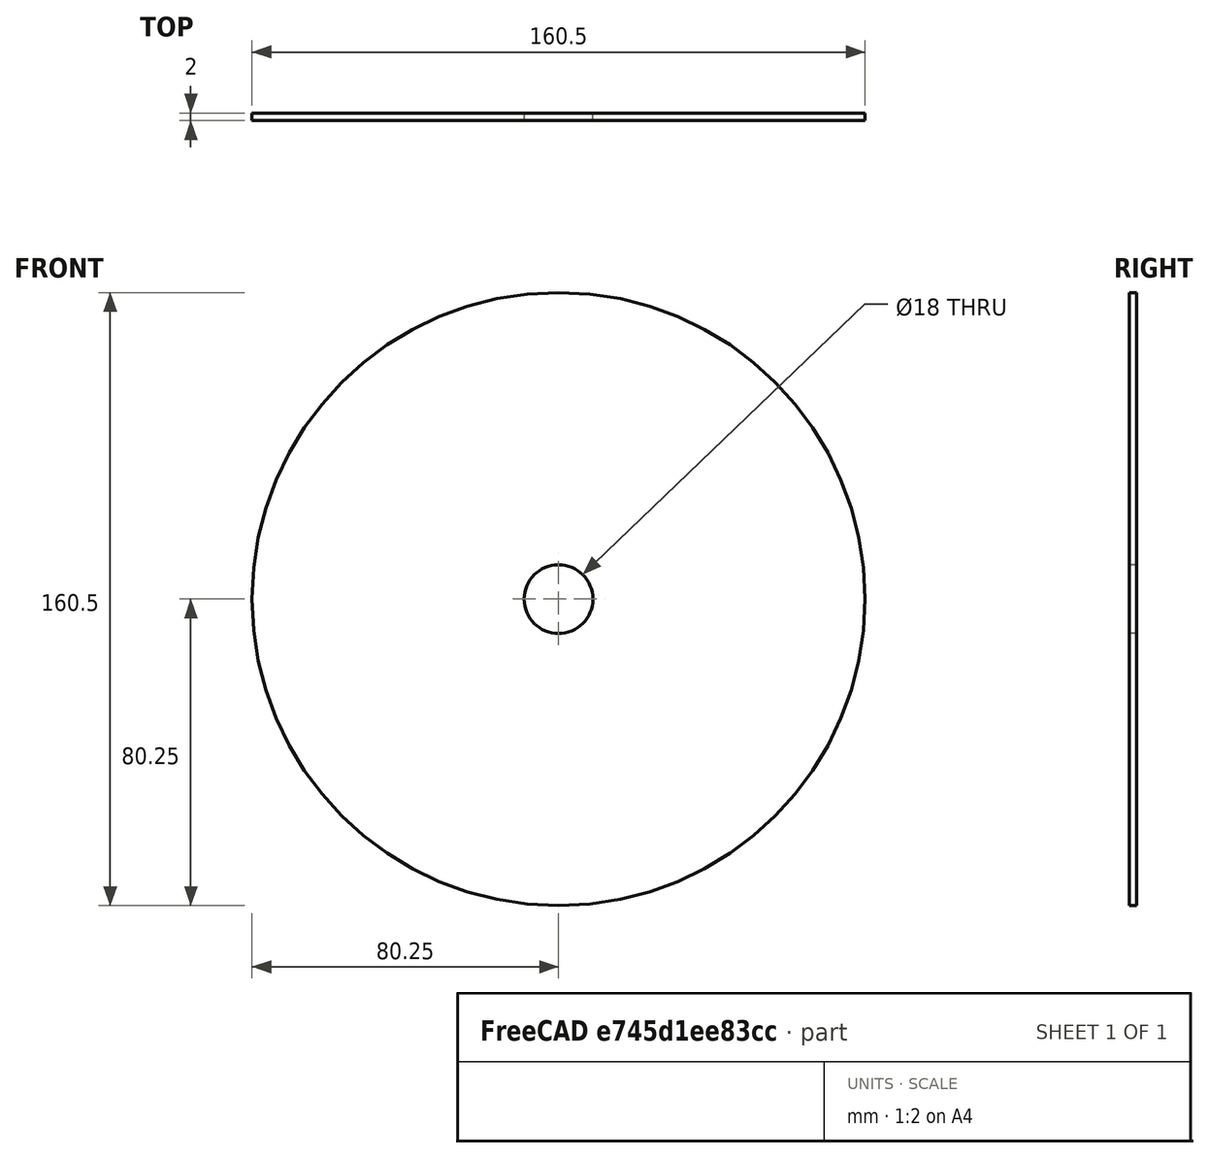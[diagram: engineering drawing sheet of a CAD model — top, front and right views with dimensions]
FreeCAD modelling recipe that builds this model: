
FCSTD DOCUMENT  (FreeCAD 0.21R33771 (Git))
Label: e1a24e2bb6364e30
License: All rights reserved
LicenseURL: https://en.wikipedia.org/wiki/All_rights_reserved
objects: Sketcher::SketchObject×2, TechDraw::DrawSVGTemplate×2, TechDraw::DrawViewPart×2, TechDraw::DrawPage×2, TechDraw::DrawViewDimExtent×2, Spreadsheet::Sheet×1, PartDesign::Pad×1, PartDesign::Pocket×1, PartDesign::Body×1
note: 9 computed .brp shape members not serialized (recipe doc carries the construction recipe); baked Part::Feature solids carry a one-line shape summary decoded from their .brp

FEATURE [Spreadsheet::Sheet] Spreadsheet  label="specification"
  cells = A1='Name ; B1(name)='Sägeblatt; A2='Beschreibung ; B2(description)='Sägeblatt für Harthölzer; A3='Typ ; B3(type)='SBHH; A4='Stammblattbreite (mm) ; B4(stammblattbreite)=2; A5='Plattensitzhöhe (mm) ; B5(plattensitzhoehe)=3.5; A6='Plattensitzlänge (mm) ; B6(plattensitzlaenge)=3.55; A7='Plattensitzwinkel (°) ; B7(plattensitzwinkel)=40.25; A8='Schnittbreite (mm) ; B8(schnittbreite)=3.2; A9='Außendurchmesser (mm) ; B9(aussendurchmesser)=160.5; A10='Bohrungsdurchmesser (mm) ; B10(bohrungsdurchmesser)=18; A11='Zähnezahl ; B11(zaehnezahl)=60
FEATURE [Sketcher::SketchObject] Sketch
  FullyConstrained = true
  MapMode = 5
  Placement = pos=(0,0,0) rot=(1,0,0;1.5708rad)
  Support = -> [XZ_Plane]
  expr: Constraints[1] = Spreadsheet.aussendurchmesser
  sketch-geometry (1):
    g0: Circle CenterX=0 CenterY=0 CenterZ=0 NormalX=0 NormalY=0 NormalZ=1 AngleXU=0 Radius=80.25
  constraints (2):
    c: Coincident(g0,g-1)
    c: Diameter(g0) = 160.5
FEATURE [PartDesign::Pad] Pad
  Direction = (0,-1,-2e-16)
  Length = 2
  Length2 = 10
  Placement = pos=(0,0,0) rot=(1,0,0;1.5708rad)
  Profile = -> Sketch
  ReferenceAxis = -> Sketch [N_Axis]
  Type = 0
  expr: Length = Spreadsheet.stammblattbreite
FEATURE [Sketcher::SketchObject] Sketch001
  FullyConstrained = true
  MapMode = 5
  Placement = pos=(0,0,0) rot=(1,0,0;1.5708rad)
  Support = -> [XZ_Plane]
  expr: Constraints[1] = Spreadsheet.bohrungsdurchmesser
  sketch-geometry (1):
    g0: Circle CenterX=0 CenterY=0 CenterZ=0 NormalX=0 NormalY=0 NormalZ=1 AngleXU=0 Radius=9
  constraints (2):
    c: Coincident(g0,g-1)
    c: Diameter(g0) = 18
FEATURE [PartDesign::Pocket] Pocket
  BaseFeature = -> Pad
  Direction = (0,1,2e-16)
  Length = 5
  Length2 = 5
  Midplane = true
  Placement = pos=(0,0,0) rot=(1,0,0;1.5708rad)
  Profile = -> Sketch001
  ReferenceAxis = -> Sketch001 [N_Axis]
  Type = 1
FEATURE [PartDesign::Body] Body  label="Körper"
  Group = -> [Sketch,Pad,Sketch001,Pocket]
  Origin = -> Origin
  Tip = -> Pocket
FEATURE [TechDraw::DrawSVGTemplate] Template
  Height = 841
  Orientation = 1
  Template = C:/Program Files/FreeCAD 0.21/data/Mod/TechDraw/Templates/A0_Landscape_blank.svg
  Width = 1189
FEATURE [TechDraw::DrawViewPart] View
  CoarseView = false
  Direction = (0,-1,0)
  Focus = 100
  HardHidden = false
  IsoCount = 0
  IsoHidden = false
  IsoVisible = false
  LockPosition = false
  Perspective = false
  Rotation = 0
  ScaleType = 0
  ScrubCount = 0
  SeamHidden = false
  SeamVisible = false
  SmoothHidden = false
  SmoothVisible = true
  Source = -> [Body]
  X = 594.5
  XDirection = (1,0,0)
  Y = 420.5
FEATURE [TechDraw::DrawPage] Page  label="dxfexport"
  KeepUpdated = true
  NextBalloonIndex = 1
  ProjectionType = 0
  Template = -> Template
  Views = -> [View]
FEATURE [TechDraw::DrawSVGTemplate] Template001
  EditableTexts = Designed_by_Name=Designed by Name; Drawing_number=Drawing number; FC-Date=Date; FC-SC=Scale; FC-SH=Sheet; FC-Title=Title; Subtitle=Subtitle; Weight=Weight
  Height = 210
  Orientation = 1
  Template = C:/Program Files/FreeCAD 0.21/data/Mod/TechDraw/Templates/A4_LandscapeTD.svg
  Width = 297
FEATURE [TechDraw::DrawViewPart] View001
  CoarseView = false
  Direction = (0,-1,0)
  Focus = 100
  HardHidden = false
  IsoCount = 0
  IsoHidden = false
  IsoVisible = false
  LockPosition = false
  Perspective = false
  Rotation = 0
  Scale = 0.5
  ScaleType = 2
  ScrubCount = 0
  SeamHidden = false
  SeamVisible = false
  SmoothHidden = false
  SmoothVisible = true
  Source = -> [Body]
  X = 148.5
  XDirection = (1,0,0)
  Y = 105
FEATURE [TechDraw::DrawViewDimExtent] DimExtent
  AngleOverride = false
  Arbitrary = false
  ArbitraryTolerances = false
  DirExtent = 0
  EqualTolerance = true
  ExtensionAngle = 0
  FormatSpec = %.2w
  FormatSpecOverTolerance = %+.2w
  FormatSpecUnderTolerance = %+.2w
  Inverted = false
  LineAngle = 0
  LockPosition = false
  MeasureType = 1
  OverTolerance = 0
  References2D = -> [View001]
  Rotation = 0
  ScaleType = 0
  Source = -> [View001]
  TheoreticalExact = false
  Type = 1
  UnderTolerance = 0
  X = -0.897436
  Y = 70.8974
FEATURE [TechDraw::DrawViewDimExtent] DimExtent001
  AngleOverride = false
  Arbitrary = false
  ArbitraryTolerances = false
  DirExtent = 0
  EqualTolerance = true
  ExtensionAngle = 0
  FormatSpec = %.2w
  FormatSpecOverTolerance = %+.2w
  FormatSpecUnderTolerance = %+.2w
  Inverted = false
  LineAngle = 0
  LockPosition = false
  MeasureType = 1
  OverTolerance = 0
  References2D = -> [View001]
  Rotation = 0
  ScaleType = 0
  Source = -> [View001]
  TheoreticalExact = false
  Type = 1
  UnderTolerance = 0
  X = 0
  Y = -7.17949
FEATURE [TechDraw::DrawPage] Page001  label="technical-drawing"
  KeepUpdated = true
  NextBalloonIndex = 1
  ProjectionType = 0
  Template = -> Template001
  Views = -> [View001,DimExtent,DimExtent001]
